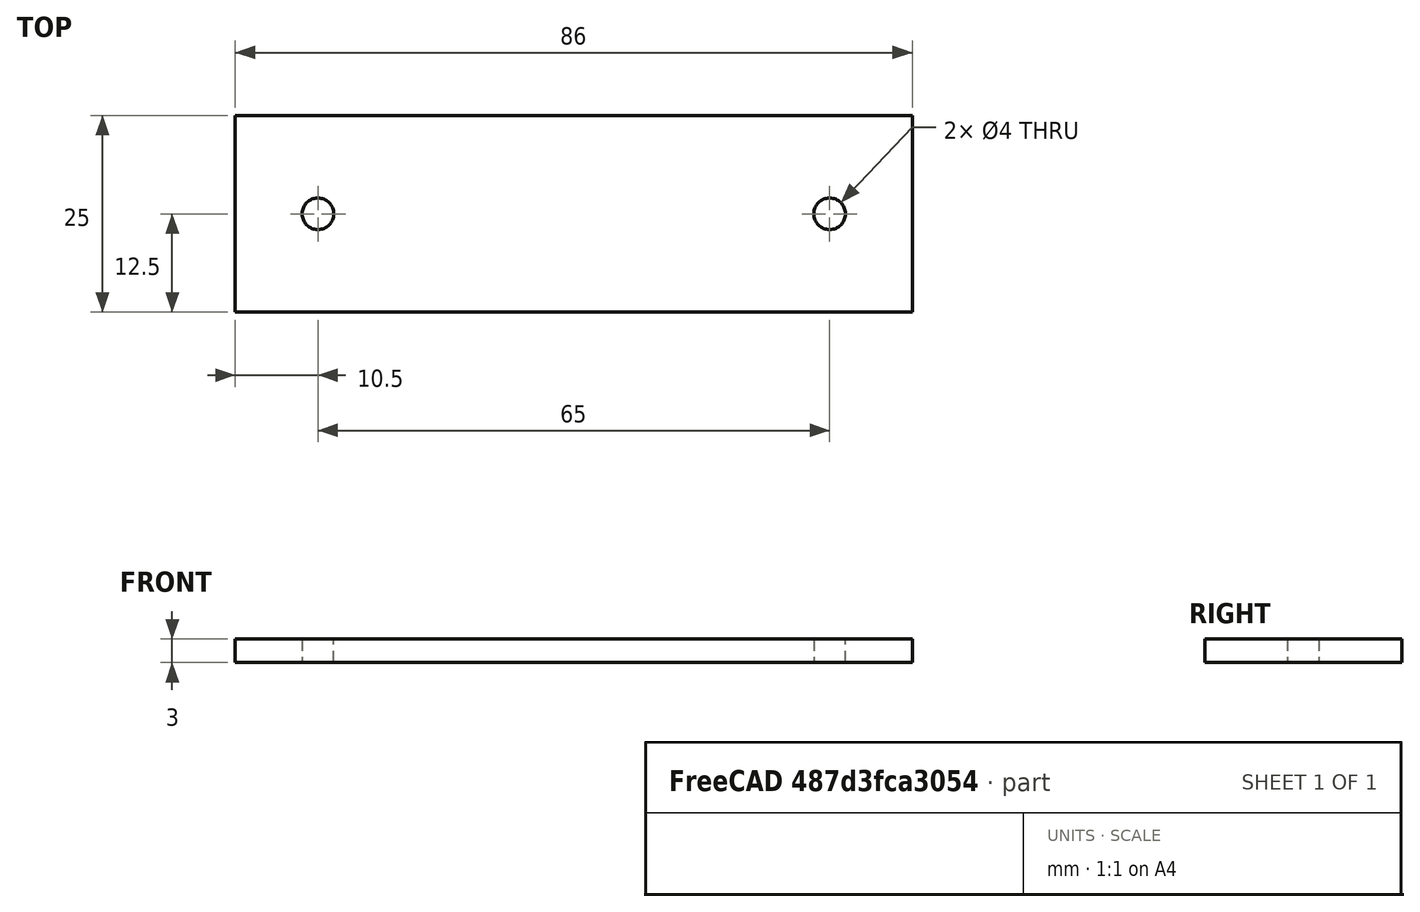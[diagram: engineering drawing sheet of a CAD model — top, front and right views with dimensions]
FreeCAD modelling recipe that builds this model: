
FCSTD DOCUMENT  (FreeCAD 0.16R6705 (Git))
Label: p3x050u01
License: All rights reserved
LicenseURL: http://en.wikipedia.org/wiki/All_rights_reserved
objects: Sketcher::SketchObject×1, PartDesign::Pad×1
note: 3 computed .brp shape members not serialized (recipe doc carries the construction recipe); baked Part::Feature solids carry a one-line shape summary decoded from their .brp

FEATURE [Sketcher::SketchObject] Sketch
  sketch-geometry (6):
    g0: LineSegment StartX=-43 StartY=12.5 StartZ=0 EndX=43 EndY=12.5 EndZ=0
    g1: LineSegment StartX=43 StartY=12.5 StartZ=0 EndX=43 EndY=-12.5 EndZ=0
    g2: LineSegment StartX=43 StartY=-12.5 StartZ=0 EndX=-43 EndY=-12.5 EndZ=0
    g3: LineSegment StartX=-43 StartY=-12.5 StartZ=0 EndX=-43 EndY=12.5 EndZ=0
    g4: Circle CenterX=-32.5 CenterY=0 CenterZ=0 NormalX=0 NormalY=0 NormalZ=1 Radius=2
    g5: Circle CenterX=32.5 CenterY=0 CenterZ=0 NormalX=0 NormalY=0 NormalZ=1 Radius=2
  constraints (18):
    c: Coincident(g0,g1)
    c: Coincident(g1,g2)
    c: Coincident(g2,g3)
    c: Coincident(g3,g0)
    c: Horizontal(g0)
    c: Horizontal(g2)
    c: Vertical(g1)
    c: Vertical(g3)
    c: Symmetric(g0,g0,g-2)
    c: Symmetric(g0,g2,g-1)
    c: Distance(g0) = 86
    c: Distance(g3) = 25
    c: PointOnObject(g4,g-1)
    c: PointOnObject(g5,g-1)
    c: Equal(g4,g5)
    c: Symmetric(g4,g5,g-2)
    c: DistanceX(g4,g5) = 65
    c: Radius(g4) = 2
FEATURE [PartDesign::Pad] Pad
  Length = 3
  Length2 = 100
  Sketch = -> Sketch
  Type = 0
